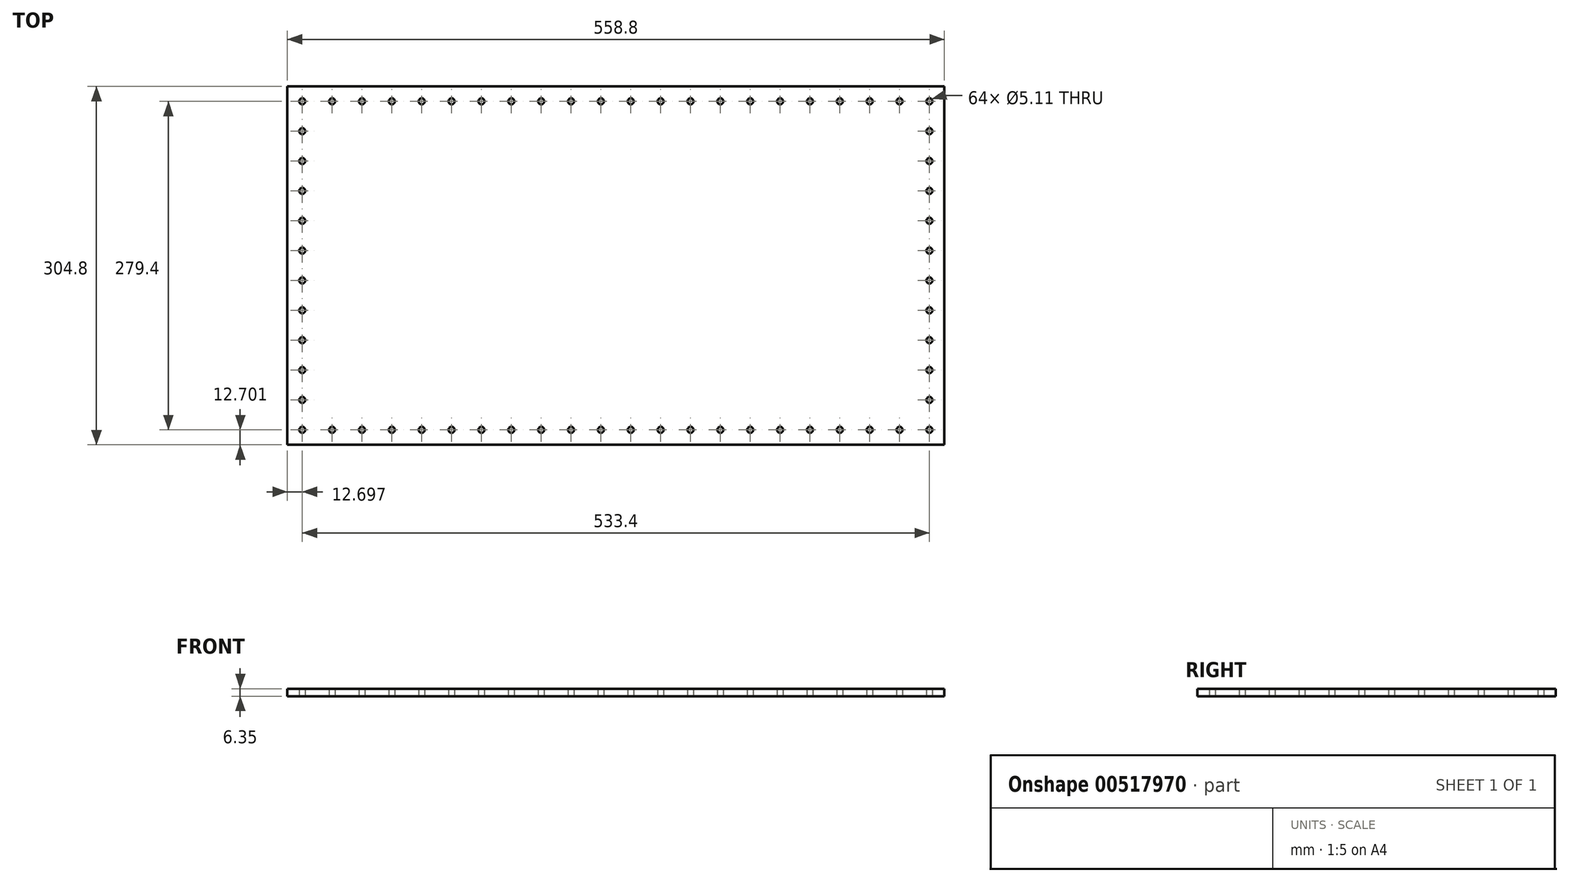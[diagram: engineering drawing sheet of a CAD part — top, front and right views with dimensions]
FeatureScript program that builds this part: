
annotation { "Feature Type Name" : "Feature", "Feature Type Description" : "" }
export const myFeature = defineFeature(function(context is Context, id is Id, definition is map)
    precondition{}
    {
        {
            var Q0;
            Q0=qCreatedBy(makeId("Top.planeOp"),FACE);
            var sketch = newSketch(context, id + "F0", { "sketchPlane" : qUnion([Q0])});
            skLineSegment(sketch, "E0.bottom", {"start": v(-179.94, 150.42) * mm, "end": v(378.86, 150.42) * mm});
            skLineSegment(sketch, "E0.top", {"start": v(-179.94, -154.38) * mm, "end": v(378.86, -154.38) * mm});
            skLineSegment(sketch, "E0.left", {"start": v(-179.94, 150.42) * mm, "end": v(-179.94, -154.38) * mm});
            skLineSegment(sketch, "E0.right", {"start": v(378.86, 150.42) * mm, "end": v(378.86, -154.38) * mm});
            skCircle(sketch, "E1", {"center": v(-167.24, 137.72) * mm, "radius": 2.55 * mm});
            skCircle(sketch, "E2.1.0.0", {"center": v(-141.84, 137.72) * mm, "radius": 2.55 * mm});
            skCircle(sketch, "E2.2.0.0", {"center": v(-116.44, 137.72) * mm, "radius": 2.55 * mm});
            skCircle(sketch, "E2.3.0.0", {"center": v(-91.04, 137.72) * mm, "radius": 2.55 * mm});
            skCircle(sketch, "E2.4.0.0", {"center": v(-65.64, 137.72) * mm, "radius": 2.55 * mm});
            skCircle(sketch, "E2.5.0.0", {"center": v(-40.24, 137.72) * mm, "radius": 2.55 * mm});
            skCircle(sketch, "E2.6.0.0", {"center": v(-14.84, 137.72) * mm, "radius": 2.55 * mm});
            skCircle(sketch, "E2.7.0.0", {"center": v(10.56, 137.72) * mm, "radius": 2.55 * mm});
            skCircle(sketch, "E2.8.0.0", {"center": v(35.96, 137.72) * mm, "radius": 2.55 * mm});
            skCircle(sketch, "E2.9.0.0", {"center": v(61.36, 137.72) * mm, "radius": 2.55 * mm});
            skCircle(sketch, "E2.10.0.0", {"center": v(86.76, 137.72) * mm, "radius": 2.55 * mm});
            skCircle(sketch, "E2.11.0.0", {"center": v(112.16, 137.72) * mm, "radius": 2.55 * mm});
            skCircle(sketch, "E2.12.0.0", {"center": v(137.56, 137.72) * mm, "radius": 2.55 * mm});
            skCircle(sketch, "E2.13.0.0", {"center": v(162.96, 137.72) * mm, "radius": 2.55 * mm});
            skCircle(sketch, "E2.14.0.0", {"center": v(188.36, 137.72) * mm, "radius": 2.55 * mm});
            skCircle(sketch, "E2.15.0.0", {"center": v(213.76, 137.72) * mm, "radius": 2.55 * mm});
            skCircle(sketch, "E2.16.0.0", {"center": v(239.16, 137.72) * mm, "radius": 2.55 * mm});
            skCircle(sketch, "E2.17.0.0", {"center": v(264.56, 137.72) * mm, "radius": 2.55 * mm});
            skCircle(sketch, "E2.18.0.0", {"center": v(289.96, 137.72) * mm, "radius": 2.55 * mm});
            skCircle(sketch, "E2.19.0.0", {"center": v(315.36, 137.72) * mm, "radius": 2.55 * mm});
            skCircle(sketch, "E2.20.0.0", {"center": v(340.76, 137.72) * mm, "radius": 2.55 * mm});
            skCircle(sketch, "E2.21.0.0", {"center": v(366.16, 137.72) * mm, "radius": 2.55 * mm});
            skLineSegment(sketch, "E2.direction1", {"start": v(-167.24, 137.72) * mm, "end": v(-141.84, 137.72) * mm, "construction": true});
            skCircle(sketch, "E3.0.1.0", {"center": v(366.16, 112.32) * mm, "radius": 2.55 * mm});
            skCircle(sketch, "E3.0.2.0", {"center": v(366.16, 86.92) * mm, "radius": 2.55 * mm});
            skCircle(sketch, "E3.0.3.0", {"center": v(366.16, 61.52) * mm, "radius": 2.55 * mm});
            skCircle(sketch, "E3.0.4.0", {"center": v(366.16, 36.12) * mm, "radius": 2.55 * mm});
            skCircle(sketch, "E3.0.5.0", {"center": v(366.16, 10.72) * mm, "radius": 2.55 * mm});
            skCircle(sketch, "E3.0.6.0", {"center": v(366.16, -14.68) * mm, "radius": 2.55 * mm});
            skCircle(sketch, "E3.0.7.0", {"center": v(366.16, -40.08) * mm, "radius": 2.55 * mm});
            skCircle(sketch, "E3.0.8.0", {"center": v(366.16, -65.48) * mm, "radius": 2.55 * mm});
            skCircle(sketch, "E3.0.9.0", {"center": v(366.16, -90.88) * mm, "radius": 2.55 * mm});
            skCircle(sketch, "E3.0.10.0", {"center": v(366.16, -116.28) * mm, "radius": 2.55 * mm});
            skCircle(sketch, "E3.0.11.0", {"center": v(366.16, -141.68) * mm, "radius": 2.55 * mm});
            skLineSegment(sketch, "E3.direction1", {"start": v(366.16, 137.72) * mm, "end": v(391.56, 137.72) * mm, "construction": true});
            skLineSegment(sketch, "E3.direction2", {"start": v(366.16, 137.72) * mm, "end": v(366.16, 112.32) * mm, "construction": true});
            skCircle(sketch, "E4.1.0.0", {"center": v(340.76, -141.68) * mm, "radius": 2.55 * mm});
            skCircle(sketch, "E4.2.0.0", {"center": v(315.36, -141.68) * mm, "radius": 2.55 * mm});
            skCircle(sketch, "E4.3.0.0", {"center": v(289.96, -141.68) * mm, "radius": 2.55 * mm});
            skCircle(sketch, "E4.4.0.0", {"center": v(264.56, -141.68) * mm, "radius": 2.55 * mm});
            skCircle(sketch, "E4.5.0.0", {"center": v(239.16, -141.68) * mm, "radius": 2.55 * mm});
            skCircle(sketch, "E4.6.0.0", {"center": v(213.76, -141.68) * mm, "radius": 2.55 * mm});
            skCircle(sketch, "E4.7.0.0", {"center": v(188.36, -141.68) * mm, "radius": 2.55 * mm});
            skCircle(sketch, "E4.8.0.0", {"center": v(162.96, -141.68) * mm, "radius": 2.55 * mm});
            skCircle(sketch, "E4.9.0.0", {"center": v(137.56, -141.68) * mm, "radius": 2.55 * mm});
            skCircle(sketch, "E4.10.0.0", {"center": v(112.16, -141.68) * mm, "radius": 2.55 * mm});
            skCircle(sketch, "E4.11.0.0", {"center": v(86.76, -141.68) * mm, "radius": 2.55 * mm});
            skCircle(sketch, "E4.12.0.0", {"center": v(61.36, -141.68) * mm, "radius": 2.55 * mm});
            skCircle(sketch, "E4.13.0.0", {"center": v(35.96, -141.68) * mm, "radius": 2.55 * mm});
            skCircle(sketch, "E4.14.0.0", {"center": v(10.56, -141.68) * mm, "radius": 2.55 * mm});
            skCircle(sketch, "E4.15.0.0", {"center": v(-14.84, -141.68) * mm, "radius": 2.55 * mm});
            skCircle(sketch, "E4.16.0.0", {"center": v(-40.24, -141.68) * mm, "radius": 2.55 * mm});
            skCircle(sketch, "E4.17.0.0", {"center": v(-65.64, -141.68) * mm, "radius": 2.55 * mm});
            skCircle(sketch, "E4.18.0.0", {"center": v(-91.04, -141.68) * mm, "radius": 2.55 * mm});
            skCircle(sketch, "E4.19.0.0", {"center": v(-116.44, -141.68) * mm, "radius": 2.55 * mm});
            skCircle(sketch, "E4.20.0.0", {"center": v(-141.84, -141.68) * mm, "radius": 2.55 * mm});
            skCircle(sketch, "E4.21.0.0", {"center": v(-167.24, -141.68) * mm, "radius": 2.55 * mm});
            skLineSegment(sketch, "E4.direction1", {"start": v(366.16, -141.68) * mm, "end": v(340.76, -141.68) * mm, "construction": true});
            skCircle(sketch, "E5.0.1.0", {"center": v(-167.24, -116.28) * mm, "radius": 2.55 * mm});
            skCircle(sketch, "E5.0.2.0", {"center": v(-167.24, -90.88) * mm, "radius": 2.55 * mm});
            skCircle(sketch, "E5.0.3.0", {"center": v(-167.24, -65.48) * mm, "radius": 2.55 * mm});
            skCircle(sketch, "E5.0.4.0", {"center": v(-167.24, -40.08) * mm, "radius": 2.55 * mm});
            skCircle(sketch, "E5.0.5.0", {"center": v(-167.24, -14.68) * mm, "radius": 2.55 * mm});
            skCircle(sketch, "E5.0.6.0", {"center": v(-167.24, 10.72) * mm, "radius": 2.55 * mm});
            skCircle(sketch, "E5.0.7.0", {"center": v(-167.24, 36.12) * mm, "radius": 2.55 * mm});
            skCircle(sketch, "E5.0.8.0", {"center": v(-167.24, 61.52) * mm, "radius": 2.55 * mm});
            skCircle(sketch, "E5.0.9.0", {"center": v(-167.24, 86.92) * mm, "radius": 2.55 * mm});
            skCircle(sketch, "E5.0.10.0", {"center": v(-167.24, 112.32) * mm, "radius": 2.55 * mm});
            skLineSegment(sketch, "E5.direction1", {"start": v(-167.24, -141.68) * mm, "end": v(-141.84, -141.68) * mm, "construction": true});
            skLineSegment(sketch, "E5.direction2", {"start": v(-167.24, -141.68) * mm, "end": v(-167.24, -116.28) * mm, "construction": true});
            skSolve(sketch);
        }
        {
            var Q0;
            Q0 = qSketchRegion(id + "F0", true);
            var Q1;
            Q1=makeQuery(id+"F0.imprint","IMPRINT",FACE,{"disambiguationData":[TD([[makeQuery(id+"F0.imprint","IMPRINT",EDGE,{"derivedFrom":sQuery(id+"F0.wireOp",EDGE,"E0.bottom")}),-1.0]])]});
            extrude(context, id + "F1", {"entities" : qUnion([Q0, Q1]), "depth" : 6.35 * mm, "offsetDistance" : 25.4 * mm});
        }
    });
